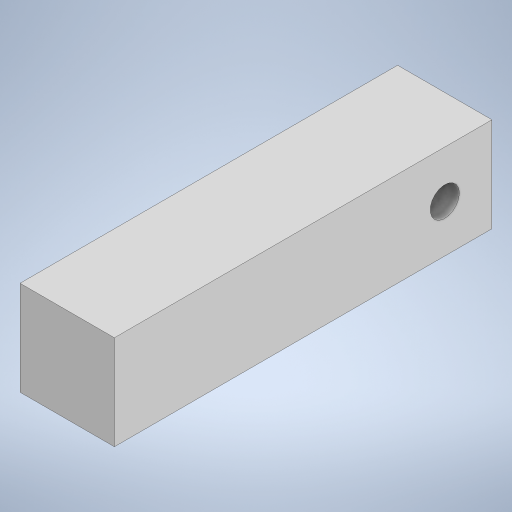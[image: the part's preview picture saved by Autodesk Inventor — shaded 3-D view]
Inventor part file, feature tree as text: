
AUTODESK INVENTOR PART (.ipt)
format: ipt  version: 2023 (Build 270158000, 158)  size: 195,072 bytes
history: native  units: mm
features: sketch x2, other x1, extrude x1, hole x1
ambient origin geometry x8: Origin, YZ Plane, XZ Plane, XY Plane, X Axis, Y Axis, Z Axis, Center Point
bodies: Body1 (feature_tree)
feature tree (5):
  other  "ソリッド1"
  extrude  "押し出し1"  Depth=10.0mm
  hole  "穴1"  [1 undecoded]
  sketch  "スケッチ1"
  sketch  "スケッチ2"
note: 1 required parameter value undecoded (feature->parameter linkage not recoverable at this tier; creation-order binding heuristic only, values carry confidence <= 0.55)
